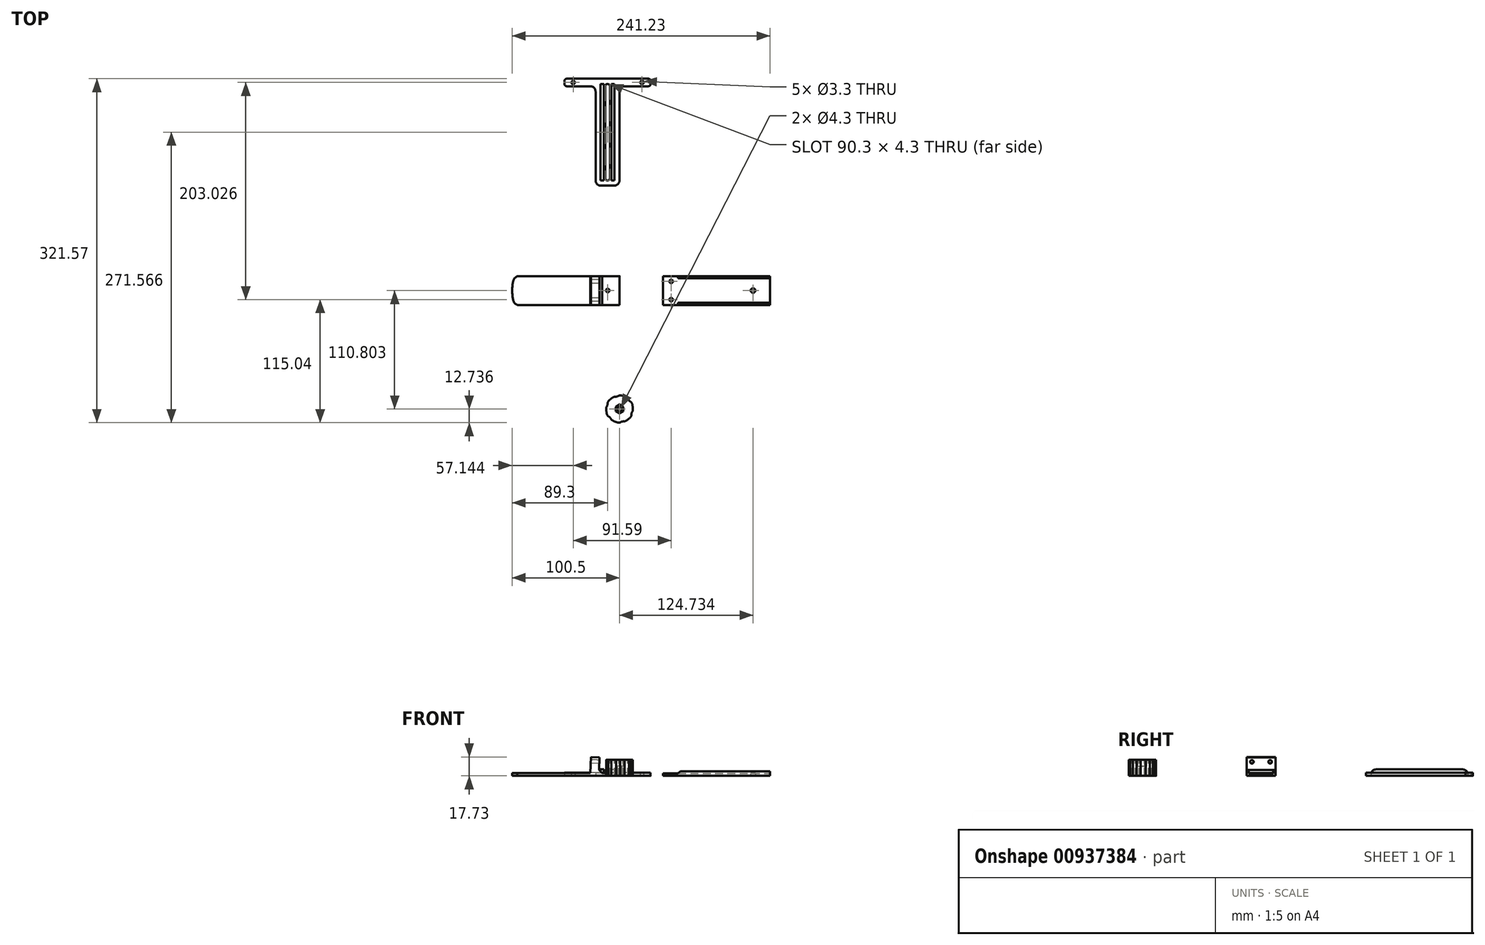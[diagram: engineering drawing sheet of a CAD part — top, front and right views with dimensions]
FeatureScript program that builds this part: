
annotation { "Feature Type Name" : "Feature", "Feature Type Description" : "" }
export const myFeature = defineFeature(function(context is Context, id is Id, definition is map)
    precondition{}
    {
        {
            var Q0;
            Q0=qCreatedBy(makeId("Top.planeOp"),FACE);
            var sketch = newSketch(context, id + "F0", { "sketchPlane" : qUnion([Q0])});
            skLineSegment(sketch, "E0.bottom", {"start": v(0, 0) * mm, "end": v(-95.5, 0) * mm});
            skLineSegment(sketch, "E0.top", {"start": v(0, -27) * mm, "end": v(-95.5, -27) * mm});
            skLineSegment(sketch, "E0.left", {"start": v(0, 0) * mm, "end": v(0, -27) * mm});
            skLineSegment(sketch, "E0.right", {"start": v(-95.5, 0) * mm, "end": v(-95.5, -27) * mm});
            skPoint(sketch, "E1", {"position": v(-100.5, -13.5) * mm});
            skPoint(sketch, "E1.positionSnap0", {"position": v(-95.5, -13.5) * mm});
            skPoint(sketch, "E2", {"position": v(-98.5, -24.5) * mm});
            skFitSpline(sketch, "E3", {"points": [v(-95.5, -27) * mm, v(-98.5, -24.5) * mm, v(-100.5, -13.5) * mm], "startDerivative": vector(-8.63, 5.95) * mm, "endDerivative": vector(-1.88, 19.98) * mm});
            skLineSegment(sketch, "E4", {"start": v(-100.5, -13.5) * mm, "end": v(-95.5, -13.5) * mm, "construction": true});
            skFitSpline(sketch, "E5.MirrorCS", {"points": [v(-95.5, 0) * mm, v(-98.5, -2.5) * mm, v(-100.5, -13.5) * mm], "startDerivative": vector(-8.63, -5.95) * mm, "endDerivative": vector(-1.88, -19.98) * mm});
            skCircle(sketch, "E6", {"center": v(-11, -13.5) * mm, "radius": 1.65 * mm});
            skPoint(sketch, "E6.centerSnap0", {"position": v(0, -13.5) * mm});
            skSolve(sketch);
        }
        {
            var Q0;
            Q0=makeQuery(id+"F0.imprint","IMPRINT",FACE,{"disambiguationData":[TD([[makeQuery(id+"F0.imprint","IMPRINT",EDGE,{"derivedFrom":sQuery(id+"F0.wireOp",EDGE,"E0.bottom")}),1.0]])]});
            var Q1;
            Q1=makeQuery(id+"F0.imprint","IMPRINT",FACE,{"disambiguationData":[TD([[makeQuery(id+"F0.imprint","IMPRINT",EDGE,{"derivedFrom":sQuery(id+"F0.wireOp",EDGE,"E0.right")}),-1.0]])]});
            extrude(context, id + "F1", {"entities" : qUnion([Q0, Q1]), "depth" : 2.5 * mm, "offsetDistance" : 25 * mm});
        }
        {
            var Q0;
            Q0=makeQuery(id+"F1.opExtrude","CAP_EDGE",EDGE,{"disambiguationData":[OSD([sQuery(id+"F0.wireOp",EDGE,"E0.left")])],"isStart":false});
            fillet(context, id + "F2", {"entities" : qUnion([Q0]), "radius" : 0.5 * mm, "tangentPropagation" : true, "allowEdgeOverflow" : false});
        }
        {
            var Q0;
            Q0=makeQuery(id+"F1.opExtrude","CAP_FACE",FACE,{"disambiguationData":[OSD([sQuery(id+"F0.wireOp",EDGE,"E0.bottom"),sQuery(id+"F0.wireOp",EDGE,"E0.top"),sQuery(id+"F0.wireOp",EDGE,"E0.left"),sQuery(id+"F0.wireOp",EDGE,"E3"),sQuery(id+"F0.wireOp",EDGE,"E5.MirrorCS"),sQuery(id+"F0.wireOp",EDGE,"E6")])],"isStart":false});
            var sketch = newSketch(context, id + "F3", { "sketchPlane" : qUnion([Q0])});
            skLineSegment(sketch, "E7.bottom", {"start": v(-20, -27) * mm, "end": v(-24, -27) * mm});
            skLineSegment(sketch, "E7.top", {"start": v(-20, 0) * mm, "end": v(-24, 0) * mm});
            skLineSegment(sketch, "E7.left", {"start": v(-20, -27) * mm, "end": v(-20, 0) * mm});
            skLineSegment(sketch, "E7.right", {"start": v(-24, -27) * mm, "end": v(-24, 0) * mm});
            skCircle(sketch, "E8", {"center": v(-11, -13.5) * mm, "radius": 5 * mm});
            skSolve(sketch);
        }
        {
            var Q0;
            Q0=qCreatedBy(makeId("Top.planeOp"),FACE);
            var sketch = newSketch(context, id + "F4", { "sketchPlane" : qUnion([Q0])});
            skLineSegment(sketch, "E9.bottom", {"start": v(40.73, 0) * mm, "end": v(140.73, 0) * mm});
            skLineSegment(sketch, "E9.top", {"start": v(40.73, -27) * mm, "end": v(140.73, -27) * mm});
            skLineSegment(sketch, "E9.left", {"start": v(40.73, 0) * mm, "end": v(40.73, -27) * mm});
            skLineSegment(sketch, "E9.right", {"start": v(140.73, 0) * mm, "end": v(140.73, -27) * mm});
            skCircle(sketch, "E10", {"center": v(48.23, -22) * mm, "radius": 1.65 * mm});
            skCircle(sketch, "E11", {"center": v(48.23, -5) * mm, "radius": 1.65 * mm});
            skCircle(sketch, "E12", {"center": v(124.73, -13.5) * mm, "radius": 2.15 * mm});
            skPoint(sketch, "E12.centerSnap0", {"position": v(140.73, -13.5) * mm});
            skSolve(sketch);
        }
        {
            var Q0;
            Q0 = qSketchRegion(id + "F4", true);
            extrude(context, id + "F5", {"entities" : qUnion([Q0]), "depth" : 2.2 * mm, "offsetDistance" : 25 * mm});
        }
        {
            var Q0;
            Q0=makeQuery(id+"F5.opExtrude","CAP_FACE",FACE,{"disambiguationData":[OSD([sQuery(id+"F4.wireOp",EDGE,"E9.bottom"),sQuery(id+"F4.wireOp",EDGE,"E9.top"),sQuery(id+"F4.wireOp",EDGE,"E9.left"),sQuery(id+"F4.wireOp",EDGE,"E9.right"),sQuery(id+"F4.wireOp",EDGE,"E10"),sQuery(id+"F4.wireOp",EDGE,"E11")])],"isStart":false});
            var sketch = newSketch(context, id + "F6", { "sketchPlane" : qUnion([Q0])});
            skLineSegment(sketch, "E13.0", {"start": v(40.73, -2) * mm, "end": v(140.73, -2) * mm});
            skLineSegment(sketch, "E14.0", {"start": v(40.73, -25) * mm, "end": v(140.73, -25) * mm});
            skLineSegment(sketch, "E15", {"start": v(54.73, -2) * mm, "end": v(54.73, 0) * mm});
            skLineSegment(sketch, "E16", {"start": v(54.73, -25) * mm, "end": v(54.73, -27) * mm});
            skSolve(sketch);
        }
        {
            var Q0;
            {var subQ3=sQuery(id+"F6.wireOp",EDGE,"E15");Q0=makeQuery(id+"F6.imprint","IMPRINT",FACE,{"disambiguationData":[TD([[makeQuery(id+"F6.imprint","IMPRINT",EDGE,{"derivedFrom":subQ3}),-1.0]])]});}
            var Q1;
            {var subQ3=sQuery(id+"F6.wireOp",EDGE,"E16");Q1=makeQuery(id+"F6.imprint","IMPRINT",FACE,{"disambiguationData":[TD([[makeQuery(id+"F6.imprint","IMPRINT",EDGE,{"derivedFrom":subQ3}),1.0]])]});}
            extrude(context, id + "F7", {"entities" : qUnion([Q0, Q1]), "operationType" : NewBodyOperationType.ADD, "depth" : 2 * mm, "offsetDistance" : 25 * mm});
        }
        {
            var Q0;
            Q0=makeQuery(id+"F7.opExtrude","CAP_EDGE",EDGE,{"disambiguationData":[OSD([sQuery(id+"F6.wireOp",EDGE,"E15")])],"isStart":false});
            var Q1;
            Q1=makeQuery(id+"F7.opExtrude","CAP_EDGE",EDGE,{"disambiguationData":[OSD([sQuery(id+"F6.wireOp",EDGE,"E16")])],"isStart":false});
            chamfer(context, id + "F8", {"entities" : qUnion([Q0, Q1]), "width" : 2 * mm, "tangentPropagation" : true});
        }
        {
            var Q0;
            Q0=qCreatedBy(makeId("Top.planeOp"),FACE);
            var sketch = newSketch(context, id + "F9", { "sketchPlane" : qUnion([Q0])});
            skLineSegment(sketch, "E17.bottom", {"start": v(0, 84.53) * mm, "end": v(-22.4, 84.53) * mm});
            skLineSegment(sketch, "E17.top", {"start": v(0, 184.53) * mm, "end": v(-22.4, 184.53) * mm});
            skLineSegment(sketch, "E17.left", {"start": v(0, 84.53) * mm, "end": v(0, 184.53) * mm});
            skLineSegment(sketch, "E17.right", {"start": v(-22.4, 84.53) * mm, "end": v(-22.4, 184.53) * mm});
            skArc(sketch, "E18", {"start": v(-13.35, 91.53) * mm, "mid": v(-11.2, 89.38) * mm, "end": v(-9.05, 91.53) * mm});
            skPoint(sketch, "E18.centerSnap0", {"position": v(-11.2, 84.53) * mm});
            skArc(sketch, "E19", {"start": v(-9.05, 177.53) * mm, "mid": v(-11.2, 179.68) * mm, "end": v(-13.35, 177.53) * mm});
            skLineSegment(sketch, "E20", {"start": v(-11.2, 184.53) * mm, "end": v(-11.2, 162.33) * mm, "construction": true});
            skLineSegment(sketch, "E21", {"start": v(0, 184.53) * mm, "end": v(27, 184.53) * mm});
            skLineSegment(sketch, "E22", {"start": v(29, 182.53) * mm, "end": v(29, 179.53) * mm});
            skLineSegment(sketch, "E23", {"start": v(27, 177.53) * mm, "end": v(0, 177.53) * mm});
            skCircle(sketch, "E24", {"center": v(20.96, 181.03) * mm, "radius": 1.65 * mm});
            skPoint(sketch, "E24.centerSnap0", {"position": v(29, 181.03) * mm});
            skPoint(sketch, "E25.visualSharp", {"position": v(29, 177.53) * mm});
            skArc(sketch, "E25.filletArc", {"start": v(27, 177.53) * mm, "mid": v(28.41, 178.11) * mm, "end": v(29, 179.53) * mm});
            skPoint(sketch, "E26.visualSharp", {"position": v(29, 184.53) * mm});
            skArc(sketch, "E26.filletArc", {"start": v(29, 182.53) * mm, "mid": v(28.41, 183.94) * mm, "end": v(27, 184.53) * mm});
            skLineSegment(sketch, "E27.MirrorCS", {"start": v(-51.4, 182.53) * mm, "end": v(-51.4, 179.53) * mm});
            skArc(sketch, "E28.MirrorCS", {"start": v(-51.4, 182.53) * mm, "mid": v(-50.81, 183.94) * mm, "end": v(-49.4, 184.53) * mm});
            skArc(sketch, "E29.MirrorCS", {"start": v(-49.4, 177.53) * mm, "mid": v(-50.81, 178.11) * mm, "end": v(-51.4, 179.53) * mm});
            skPoint(sketch, "E30.MirrorP", {"position": v(-51.4, 181.03) * mm});
            skCircle(sketch, "E31.MirrorC", {"center": v(-43.36, 181.03) * mm, "radius": 1.65 * mm});
            skLineSegment(sketch, "E32.MirrorCS", {"start": v(-22.4, 184.53) * mm, "end": v(-49.4, 184.53) * mm});
            skLineSegment(sketch, "E33.MirrorCS", {"start": v(-49.4, 177.53) * mm, "end": v(-22.4, 177.53) * mm});
            skPoint(sketch, "E34.MirrorP", {"position": v(-51.4, 177.53) * mm});
            skPoint(sketch, "E35.MirrorP", {"position": v(-51.4, 184.53) * mm});
            skLineSegment(sketch, "E36", {"start": v(-9.05, 177.53) * mm, "end": v(-9.05, 91.53) * mm});
            skLineSegment(sketch, "E37", {"start": v(-13.35, 177.53) * mm, "end": v(-13.35, 91.53) * mm});
            skSolve(sketch);
        }
        {
            var Q0;
            {var subQ3=sQuery(id+"F9.wireOp",EDGE,"E17.bottom");Q0=makeQuery(id+"F9.imprint","IMPRINT",FACE,{"disambiguationData":[TD([[makeQuery(id+"F9.imprint","IMPRINT",EDGE,{"derivedFrom":subQ3}),-1.0]])]});}
            var Q1;
            Q1=makeQuery(id+"F9.imprint","IMPRINT",FACE,{"disambiguationData":[TD([[makeQuery(id+"F9.imprint","IMPRINT",EDGE,{"derivedFrom":sQuery(id+"F9.wireOp",EDGE,"E27.MirrorCS")}),1.0]])]});
            var Q2;
            {var subQ1=sQuery(id+"F9.wireOp",EDGE,"E21");Q2=makeQuery(id+"F9.imprint","IMPRINT",FACE,{"disambiguationData":[TD([[makeQuery(id+"F9.imprint","IMPRINT",EDGE,{"derivedFrom":subQ1}),-1.0]])]});}
            extrude(context, id + "F10", {"entities" : qUnion([Q0, Q1, Q2]), "depth" : 3 * mm, "offsetDistance" : 25 * mm});
        }
        {
            var Q0;
            Q0=makeQuery(id+"F10.opExtrude","SWEPT_EDGE",EDGE,{"disambiguationData":[OSD([sQuery(id+"F9.wireOp",EDGE,"E17.bottom"),sQuery(id+"F9.wireOp",EDGE,"E17.right")])]});
            var Q1;
            Q1=makeQuery(id+"F10.opExtrude","SWEPT_EDGE",EDGE,{"disambiguationData":[OSD([sQuery(id+"F9.wireOp",EDGE,"E17.bottom"),sQuery(id+"F9.wireOp",EDGE,"E17.left")])]});
            var Q2;
            Q2=makeQuery(id+"F10.opExtrude","SWEPT_EDGE",EDGE,{"disambiguationData":[OSD([sQuery(id+"F9.wireOp",EDGE,"E17.left"),sQuery(id+"F9.wireOp",EDGE,"E23")])]});
            var Q3;
            Q3=makeQuery(id+"F10.opExtrude","SWEPT_EDGE",EDGE,{"disambiguationData":[OSD([sQuery(id+"F9.wireOp",EDGE,"E17.right"),sQuery(id+"F9.wireOp",EDGE,"E33.MirrorCS")])]});
            fillet(context, id + "F11", {"entities" : qUnion([Q0, Q1, Q2, Q3]), "radius" : 5 * mm, "tangentPropagation" : true, "allowEdgeOverflow" : false});
        }
        {
            var Q0;
            Q0=makeQuery(id+"F10.opExtrude","CAP_FACE",FACE,{"disambiguationData":[OSD([sQuery(id+"F9.wireOp",EDGE,"E17.bottom"),sQuery(id+"F9.wireOp",EDGE,"E17.top"),sQuery(id+"F9.wireOp",EDGE,"E17.left"),sQuery(id+"F9.wireOp",EDGE,"E17.right"),sQuery(id+"F9.wireOp",EDGE,"E18"),sQuery(id+"F9.wireOp",EDGE,"E19"),sQuery(id+"F9.wireOp",EDGE,"E21"),sQuery(id+"F9.wireOp",EDGE,"E22"),sQuery(id+"F9.wireOp",EDGE,"E23"),sQuery(id+"F9.wireOp",EDGE,"E24"),sQuery(id+"F9.wireOp",EDGE,"E25.filletArc"),sQuery(id+"F9.wireOp",EDGE,"E26.filletArc"),sQuery(id+"F9.wireOp",EDGE,"E27.MirrorCS"),sQuery(id+"F9.wireOp",EDGE,"E28.MirrorCS"),sQuery(id+"F9.wireOp",EDGE,"E29.MirrorCS"),sQuery(id+"F9.wireOp",EDGE,"E31.MirrorC"),sQuery(id+"F9.wireOp",EDGE,"E32.MirrorCS"),sQuery(id+"F9.wireOp",EDGE,"E33.MirrorCS"),sQuery(id+"F9.wireOp",EDGE,"E36"),sQuery(id+"F9.wireOp",EDGE,"E37")])],"isStart":false});
            var sketch = newSketch(context, id + "F12", { "sketchPlane" : qUnion([Q0])});
            skLineSegment(sketch, "E38.0", {"start": v(-13.35, 177.53) * mm, "end": v(-13.35, 91.53) * mm});
            skLineSegment(sketch, "E39.0", {"start": v(-9.05, 177.53) * mm, "end": v(-9.05, 91.53) * mm});
            skPoint(sketch, "E40.0", {"position": v(-11.2, 179.68) * mm});
            skPoint(sketch, "E41.0", {"position": v(-11.2, 89.38) * mm});
            skLineSegment(sketch, "E42.bottom", {"start": v(-14.75, 89.53) * mm, "end": v(-7.65, 89.53) * mm});
            skLineSegment(sketch, "E42.top", {"start": v(-14.75, 179.53) * mm, "end": v(-7.65, 179.53) * mm});
            skLineSegment(sketch, "E42.left", {"start": v(-14.75, 89.53) * mm, "end": v(-14.75, 179.53) * mm});
            skLineSegment(sketch, "E42.right", {"start": v(-7.65, 89.53) * mm, "end": v(-7.65, 179.53) * mm});
            skPoint(sketch, "E42.middle", {"position": v(-11.2, 134.53) * mm});
            skPoint(sketch, "E42.middle.positionSnap0", {"position": v(-9.05, 134.53) * mm});
            skPoint(sketch, "E42.centerSnap0", {"position": v(-9.05, 134.53) * mm});
            skLineSegment(sketch, "E43.0", {"start": v(-4.65, 89.53) * mm, "end": v(-4.65, 179.53) * mm});
            skLineSegment(sketch, "E44.0", {"start": v(-17.75, 89.53) * mm, "end": v(-17.75, 179.53) * mm});
            skLineSegment(sketch, "E45", {"start": v(-4.65, 89.53) * mm, "end": v(-7.65, 89.53) * mm});
            skLineSegment(sketch, "E46", {"start": v(-14.75, 89.53) * mm, "end": v(-17.75, 89.53) * mm});
            skLineSegment(sketch, "E47", {"start": v(-17.75, 179.53) * mm, "end": v(-14.75, 179.53) * mm});
            skLineSegment(sketch, "E48", {"start": v(-7.65, 179.53) * mm, "end": v(-4.65, 179.53) * mm});
            skSolve(sketch);
        }
        {
            var Q0;
            Q0=makeQuery(id+"F12.imprint","IMPRINT",FACE,{"disambiguationData":[TD([[makeQuery(id+"F12.imprint","IMPRINT",EDGE,{"derivedFrom":sQuery(id+"F12.wireOp",EDGE,"E42.right")}),-1.0]])]});
            var Q1;
            Q1=makeQuery(id+"F12.imprint","IMPRINT",FACE,{"disambiguationData":[TD([[makeQuery(id+"F12.imprint","IMPRINT",EDGE,{"derivedFrom":sQuery(id+"F12.wireOp",EDGE,"E42.left")}),1.0]])]});
            extrude(context, id + "F13", {"entities" : qUnion([Q0, Q1]), "operationType" : NewBodyOperationType.ADD, "depth" : 3 * mm, "offsetDistance" : 25 * mm});
        }
        {
            var Q0;
            Q0=makeQuery(id+"F13.opExtrude","CAP_EDGE",EDGE,{"disambiguationData":[OSD([sQuery(id+"F12.wireOp",EDGE,"E48")])],"isStart":false});
            var Q1;
            Q1=makeQuery(id+"F13.opExtrude","CAP_EDGE",EDGE,{"disambiguationData":[OSD([sQuery(id+"F12.wireOp",EDGE,"E47")])],"isStart":false});
            var Q2;
            Q2=makeQuery(id+"F13.opExtrude","CAP_EDGE",EDGE,{"disambiguationData":[OSD([sQuery(id+"F12.wireOp",EDGE,"E45")])],"isStart":false});
            var Q3;
            Q3=makeQuery(id+"F13.opExtrude","CAP_EDGE",EDGE,{"disambiguationData":[OSD([sQuery(id+"F12.wireOp",EDGE,"E46")])],"isStart":false});
            fillet(context, id + "F14", {"entities" : qUnion([Q0, Q1, Q2, Q3]), "radius" : 5 * mm, "tangentPropagation" : true, "allowEdgeOverflow" : false});
        }
        {
            var Q0;
            Q0=qCreatedBy(makeId("Top.planeOp"),FACE);
            var sketch = newSketch(context, id + "F15", { "sketchPlane" : qUnion([Q0])});
            skCircle(sketch, "E49", {"center": v(0, -124.3) * mm, "radius": 12.5 * mm});
            skCircle(sketch, "E50", {"center": v(0, -124.3) * mm, "radius": 2.15 * mm});
            skSolve(sketch);
        }
        {
            var Q0;
            Q0=makeQuery(id+"F15.imprint","IMPRINT",FACE,{"disambiguationData":[TD([[makeQuery(id+"F15.imprint","IMPRINT",EDGE,{"derivedFrom":sQuery(id+"F15.wireOp",EDGE,"E49")}),1.0]])]});
            extrude(context, id + "F16", {"entities" : qUnion([Q0]), "depth" : 15 * mm, "offsetDistance" : 25 * mm});
        }
        {
            var Q0;
            Q0=makeQuery(id+"F16.opExtrude","CAP_FACE",FACE,{"disambiguationData":[OSD([sQuery(id+"F15.wireOp",EDGE,"E49"),sQuery(id+"F15.wireOp",EDGE,"E50")])],"isStart":false});
            var sketch = newSketch(context, id + "F17", { "sketchPlane" : qUnion([Q0])});
            skCircle(sketch, "E51.cCircle", {"center": v(0, -124.3) * mm, "radius": 3.55 * mm, "construction": true});
            skLineSegment(sketch, "E51.0", {"start": v(-3.55, -126.35) * mm, "end": v(-3.55, -122.25) * mm});
            skLineSegment(sketch, "E51.1", {"start": v(-3.55, -122.25) * mm, "end": v(0, -120.2) * mm});
            skLineSegment(sketch, "E51.2", {"start": v(0, -120.2) * mm, "end": v(3.55, -122.25) * mm});
            skLineSegment(sketch, "E51.3", {"start": v(3.55, -122.25) * mm, "end": v(3.55, -126.35) * mm});
            skLineSegment(sketch, "E51.4", {"start": v(3.55, -126.35) * mm, "end": v(0, -128.4) * mm});
            skLineSegment(sketch, "E51.5", {"start": v(0, -128.4) * mm, "end": v(-3.55, -126.35) * mm});
            skPoint(sketch, "E51.0.midPoint", {"position": v(-3.55, -124.3) * mm});
            skArc(sketch, "E52", {"start": v(12.37, -126.1) * mm, "mid": v(11.37, -127.88) * mm, "end": v(11.17, -129.91) * mm});
            skArc(sketch, "E53.1.0", {"start": v(103.02, 73.76) * mm, "mid": v(105.06, 73.79) * mm, "end": v(106.92, 74.63) * mm});
            skArc(sketch, "E53.1.1", {"start": v(110.9, 74.22) * mm, "mid": v(109.11, 76.42) * mm, "end": v(106.92, 74.63) * mm});
            skArc(sketch, "E53.2.0", {"start": v(-115.39, 52.33) * mm, "mid": v(-116.43, 54.09) * mm, "end": v(-118.1, 55.28) * mm});
            skArc(sketch, "E53.2.1", {"start": v(-119.73, 58.93) * mm, "mid": v(-120.73, 56.29) * mm, "end": v(-118.1, 55.28) * mm});
            skPoint(sketch, "E53.center", {"position": v(0, 0) * mm});
            skArc(sketch, "E54", {"start": v(8.83, -133.15) * mm, "mid": v(10.35, -131.79) * mm, "end": v(11.17, -129.91) * mm});
            skSolve(sketch);
        }
        {
            var Q0;
            Q0=makeQuery(id+"F17.imprint","IMPRINT",FACE,{"disambiguationData":[TD([[makeQuery(id+"F17.imprint","IMPRINT",EDGE,{"derivedFrom":sQuery(id+"F17.wireOp",EDGE,"E51.0")}),-1.0]])]});
            extrude(context, id + "F18", {"entities" : qUnion([Q0]), "operationType" : NewBodyOperationType.REMOVE, "oppositeDirection" : true, "depth" : 6 * mm, "offsetDistance" : 25 * mm});
        }
        {
            var Q0;
            {var subQ0=sQuery(id+"F17.wireOp",EDGE,"E52");Q0=makeQuery(id+"F17.imprint","IMPRINT",FACE,{"disambiguationData":[TD([[makeQuery(id+"F17.imprint","IMPRINT",EDGE,{"derivedFrom":subQ0}),1.0]])]});}
            extrude(context, id + "F19", {"entities" : qUnion([Q0]), "operationType" : NewBodyOperationType.REMOVE, "oppositeDirection" : true, "depth" : 25 * mm, "offsetDistance" : 25 * mm});
        }
        {
            var Q0;
            {var subQ0=sQuery(id+"F17.wireOp",EDGE,"E54");Q0=makeQuery(id+"F17.imprint","IMPRINT",FACE,{"disambiguationData":[TD([[makeQuery(id+"F17.imprint","IMPRINT",EDGE,{"derivedFrom":subQ0}),1.0]])]});}
            var Q1;
            Q1=makeQuery(id+"F16.opExtrude","CAP_FACE",FACE,{"disambiguationData":[OSD([sQuery(id+"F15.wireOp",EDGE,"E49"),sQuery(id+"F15.wireOp",EDGE,"E50")])],"isStart":true});
            extrude(context, id + "F20", {"entities" : qUnion([Q0]), "operationType" : NewBodyOperationType.ADD, "endBound" : BoundingType.UP_TO_SURFACE, "oppositeDirection" : true, "depth" : 25 * mm, "endBoundEntityFace" : qUnion([Q1]), "offsetDistance" : 25 * mm});
        }
        {
            var Q0;
            Q0=makeQuery(id+"F20.opExtrude","SWEPT_FACE",FACE,{"disambiguationData":[OSD([sQuery(id+"F17.wireOp",EDGE,"E54")])]});
            var Q1;
            Q1=makeQuery(id+"F19.boolean.opBoolean","COPY",FACE,{"derivedFrom":makeQuery(id+"F19.opExtrude","SWEPT_FACE",FACE,{"disambiguationData":[OSD([sQuery(id+"F17.wireOp",EDGE,"E52")])]})});
            var Q2;
            Q2=makeQuery(id+"F16.opExtrude","SWEPT_FACE",FACE,{"disambiguationData":[OSD([sQuery(id+"F15.wireOp",EDGE,"E50")])]});
            circularPattern(context, id + "F21", {"patternType" : PatternType.FACE, "faces" : qUnion([Q0, Q1]), "axis" : qUnion([Q2]), "angle" : 360 * degree, "instanceCount" : 6, "equalSpace" : true});
        }
        {
            var Q0;
            Q0=makeQuery(id+"Fw11raSRzn5nQlP_1.boolean.opBoolean","MERGE",FACE,{"derivedFrom":[makeQuery(id+"F1.opExtrude","SWEPT_FACE",FACE,{"disambiguationData":[OSD([sQuery(id+"F0.wireOp",EDGE,"E0.top")])]}),makeQuery(id+"Fw11raSRzn5nQlP_1.opExtrude","SWEPT_FACE",FACE,{"disambiguationData":[OSD([sQuery(id+"F3.wireOp",EDGE,"E7.bottom")])]})]});
            var sketch = newSketch(context, id + "F22", { "sketchPlane" : qUnion([Q0])});
            skLineSegment(sketch, "E55", {"start": v(-19.35, 2.46) * mm, "end": v(-18.7, 17.38) * mm});
            skLineSegment(sketch, "E56", {"start": v(-18.7, 17.38) * mm, "end": v(-26.7, 17.73) * mm});
            skLineSegment(sketch, "E57", {"start": v(-26.7, 17.73) * mm, "end": v(-27.35, 2.5) * mm});
            skLineSegment(sketch, "E58", {"start": v(-19.35, 2.46) * mm, "end": v(-27.35, 2.5) * mm});
            skPoint(sketch, "E59.0", {"position": v(-24, 2.5) * mm});
            skPoint(sketch, "E60.0", {"position": v(-20, 2.5) * mm});
            skSolve(sketch);
        }
        {
            var Q0;
            {var subQ0=sQuery(id+"F22.wireOp",EDGE,"E56");Q0=makeQuery(id+"F22.imprint","IMPRINT",FACE,{"disambiguationData":[TD([[makeQuery(id+"F22.imprint","IMPRINT",EDGE,{"derivedFrom":subQ0}),1.0]])]});}
            var Q1;
            Q1=makeQuery(id+"Fw11raSRzn5nQlP_1.boolean.opBoolean","MERGE",FACE,{"derivedFrom":[makeQuery(id+"F1.opExtrude","SWEPT_FACE",FACE,{"disambiguationData":[OSD([sQuery(id+"F0.wireOp",EDGE,"E0.bottom")])]}),makeQuery(id+"Fw11raSRzn5nQlP_1.opExtrude","SWEPT_FACE",FACE,{"disambiguationData":[OSD([sQuery(id+"F3.wireOp",EDGE,"E7.top")])]})]});
            extrude(context, id + "F23", {"entities" : qUnion([Q0]), "operationType" : NewBodyOperationType.ADD, "endBound" : BoundingType.UP_TO_SURFACE, "oppositeDirection" : true, "depth" : 25 * mm, "endBoundEntityFace" : qUnion([Q1]), "offsetDistance" : 25 * mm});
        }
        {
            var Q0;
            Q0=makeQuery(id+"F23.opExtrude","SWEPT_EDGE",EDGE,{"disambiguationData":[OSD([sQuery(id+"F0.wireOp",EDGE,"E0.top"),sQuery(id+"F22.wireOp",EDGE,"E57"),sQuery(id+"F22.wireOp",EDGE,"E58")])]});
            var Q1;
            Q1=makeQuery(id+"F23.opExtrude","SWEPT_EDGE",EDGE,{"disambiguationData":[OSD([sQuery(id+"F0.wireOp",EDGE,"E0.top"),sQuery(id+"F22.wireOp",EDGE,"E55")])]});
            chamfer(context, id + "F24", {"entities" : qUnion([Q0, Q1]), "width" : 3 * mm, "tangentPropagation" : true});
        }
        {
            var Q0;
            Q0=makeQuery(id+"F23.opExtrude","SWEPT_FACE",FACE,{"disambiguationData":[OSD([sQuery(id+"F22.wireOp",EDGE,"E57")])]});
            var sketch = newSketch(context, id + "F25", { "sketchPlane" : qUnion([Q0])});
            skCircle(sketch, "E61", {"center": v(5, 12.32) * mm, "radius": 1.65 * mm});
            skCircle(sketch, "E62", {"center": v(22, 12.32) * mm, "radius": 1.65 * mm});
            skLineSegment(sketch, "E63", {"start": v(13.5, 16.56) * mm, "end": v(13.5, 8.27) * mm, "construction": true});
            skSolve(sketch);
        }
        {
            var Q0;
            Q0=makeQuery(id+"F25.imprint","IMPRINT",FACE,{"disambiguationData":[TD([[makeQuery(id+"F25.imprint","IMPRINT",EDGE,{"derivedFrom":sQuery(id+"F25.wireOp",EDGE,"E62")}),1.0]])]});
            var Q1;
            Q1=makeQuery(id+"F25.imprint","IMPRINT",FACE,{"disambiguationData":[TD([[makeQuery(id+"F25.imprint","IMPRINT",EDGE,{"derivedFrom":sQuery(id+"F25.wireOp",EDGE,"E61")}),1.0]])]});
            extrude(context, id + "F26", {"entities" : qUnion([Q0, Q1]), "operationType" : NewBodyOperationType.REMOVE, "oppositeDirection" : true, "depth" : 25 * mm, "offsetDistance" : 25 * mm});
        }
    });
